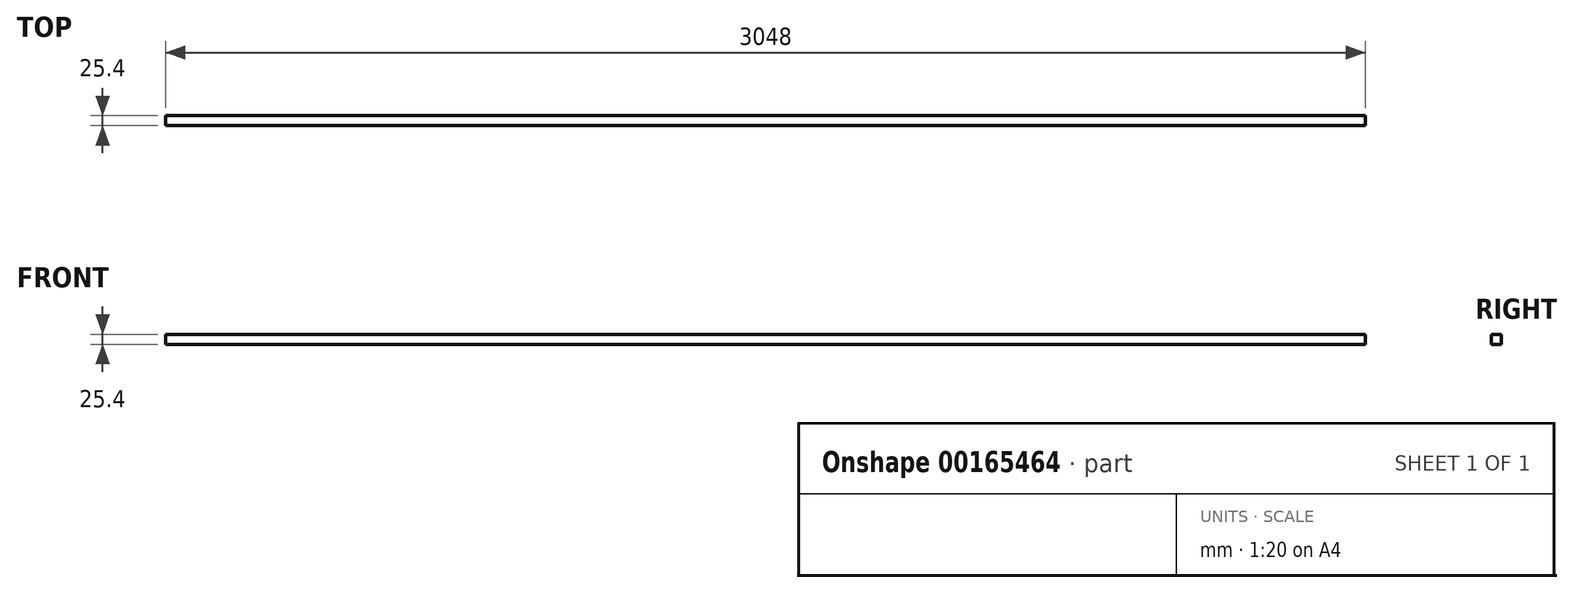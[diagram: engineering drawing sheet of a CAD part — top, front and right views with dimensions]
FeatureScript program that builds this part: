
annotation { "Feature Type Name" : "Feature", "Feature Type Description" : "" }
export const myFeature = defineFeature(function(context is Context, id is Id, definition is map)
    precondition{}
    {
        {
            var Q0;
            Q0=qCreatedBy(makeId("Right.planeOp"),FACE);
            var sketch = newSketch(context, id + "F0", { "sketchPlane" : qUnion([Q0])});
            skLineSegment(sketch, "E0.bottom", {"start": v(12.7, 12.7) * mm, "end": v(-12.7, 12.7) * mm});
            skLineSegment(sketch, "E0.top", {"start": v(12.7, -12.7) * mm, "end": v(-12.7, -12.7) * mm});
            skLineSegment(sketch, "E0.left", {"start": v(12.7, 12.7) * mm, "end": v(12.7, -12.7) * mm});
            skLineSegment(sketch, "E0.right", {"start": v(-12.7, 12.7) * mm, "end": v(-12.7, -12.7) * mm});
            skPoint(sketch, "E0.middle", {"position": v(0, 0) * mm});
            skSolve(sketch);
        }
        {
            var Q0;
            Q0 = qSketchRegion(id + "F0", true);
            extrude(context, id + "F1", {"entities" : qUnion([Q0]), "endBound" : BoundingType.SYMMETRIC, "depth" : 3048 * mm});
        }
    });
